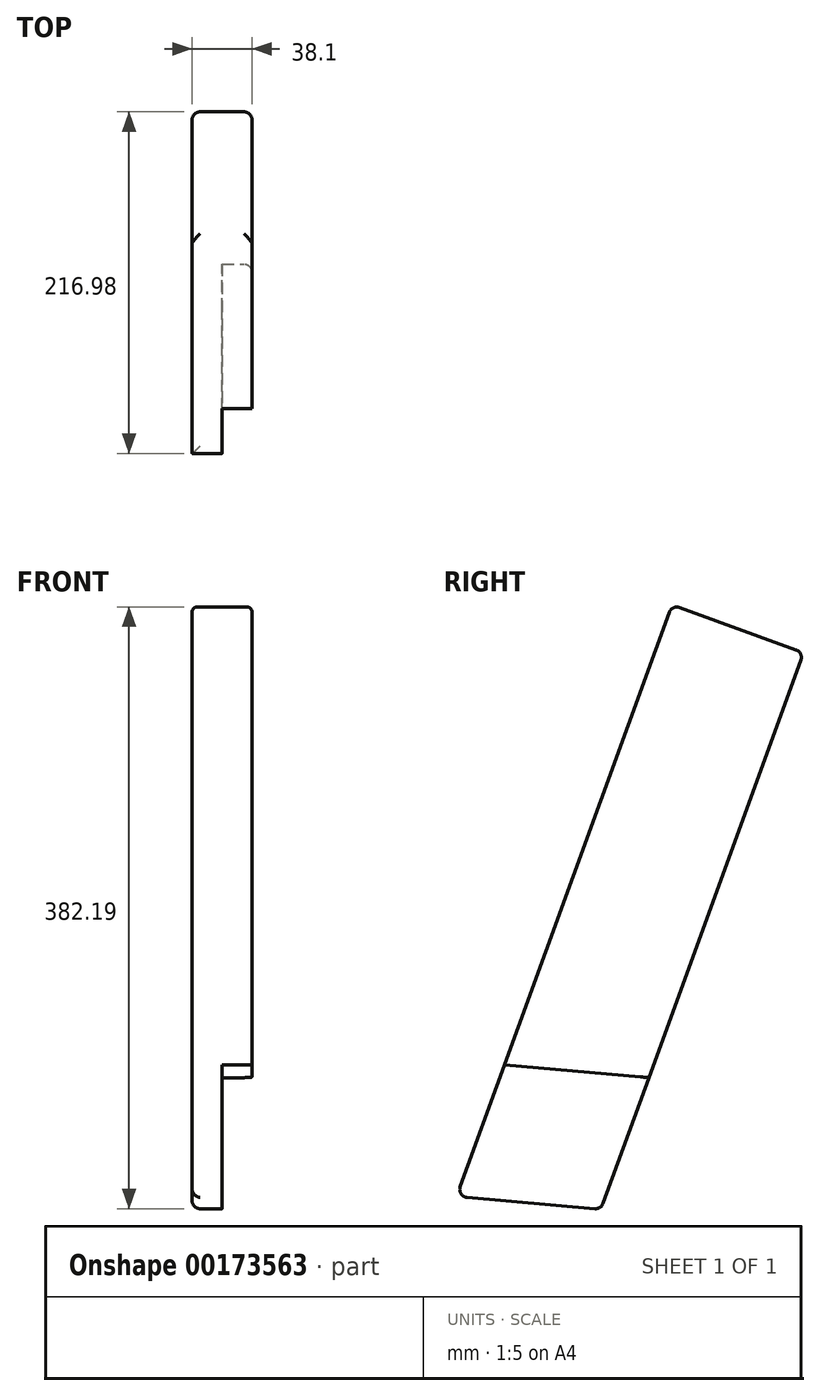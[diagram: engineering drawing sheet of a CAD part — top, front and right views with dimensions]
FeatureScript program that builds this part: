
annotation { "Feature Type Name" : "Feature", "Feature Type Description" : "" }
export const myFeature = defineFeature(function(context is Context, id is Id, definition is map)
    precondition{}
    {
        {
            var Q0;
            Q0=qCreatedBy(makeId("Right.planeOp"),FACE);
            var sketch = newSketch(context, id + "F0", { "sketchPlane" : qUnion([Q0])});
            skLineSegment(sketch, "E0", {"start": v(0, 0) * mm, "end": v(128.68, 353.54) * mm});
            skLineSegment(sketch, "E1", {"start": v(45.14, 383.95) * mm, "end": v(-91.69, 8.02) * mm});
            skLineSegment(sketch, "E2", {"start": v(-91.69, 8.02) * mm, "end": v(0, 0) * mm});
            skLineSegment(sketch, "E3", {"start": v(45.14, 383.95) * mm, "end": v(128.68, 353.54) * mm});
            skSolve(sketch);
        }
        {
            var Q0;
            Q0=makeQuery(id+"F0.imprint","IMPRINT",FACE,{"disambiguationData":[TD([[makeQuery(id+"F0.imprint","IMPRINT",EDGE,{"derivedFrom":sQuery(id+"F0.wireOp",EDGE,"E0")}),1.0]])]});
            extrude(context, id + "F1", {"entities" : qUnion([Q0]), "depth" : 38.1 * mm});
        }
        {
            var Q0;
            Q0=makeQuery(id+"F1.opExtrude","CAP_FACE",FACE,{"disambiguationData":[OSD([sQuery(id+"F0.wireOp",EDGE,"E0"),sQuery(id+"F0.wireOp",EDGE,"aKBehzrh-NYYM-WnDw-YH7h-H0UPKxIf4NXC"),sQuery(id+"F0.wireOp",EDGE,"E1"),sQuery(id+"F0.wireOp",EDGE,"E2"),sQuery(id+"F0.wireOp",EDGE,"E3")])],"isStart":false});
            var sketch = newSketch(context, id + "F2", { "sketchPlane" : qUnion([Q0])});
            skLineSegment(sketch, "E4", {"start": v(34.32, -6.04) * mm, "end": v(0, 0) * mm});
            skLineSegment(sketch, "E5", {"start": v(30.4, 83.54) * mm, "end": v(0, 0) * mm});
            skLineSegment(sketch, "E6", {"start": v(30.4, 83.54) * mm, "end": v(-61.28, 91.56) * mm});
            skLineSegment(sketch, "E7.0", {"start": v(34.32, -6.04) * mm, "end": v(-92.76, 5.07) * mm});
            skLineSegment(sketch, "E8", {"start": v(-61.28, 91.56) * mm, "end": v(-92.76, 5.07) * mm});
            skSolve(sketch);
        }
        {
            var Q0;
            Q0 = qSketchRegion(id + "F2", true);
            extrude(context, id + "F3", {"entities" : qUnion([Q0]), "operationType" : NewBodyOperationType.REMOVE, "oppositeDirection" : true, "depth" : 19.05 * mm});
        }
        {
            var Q0;
            Q0=makeQuery(id+"F1.opExtrude","SWEPT_EDGE",EDGE,{"disambiguationData":[OSD([sQuery(id+"F0.wireOp",EDGE,"aKBehzrh-NYYM-WnDw-YH7h-H0UPKxIf4NXC"),sQuery(id+"F0.wireOp",EDGE,"E3")])]});
            var Q1;
            Q1=makeQuery(id+"F1.opExtrude","CAP_EDGE",EDGE,{"disambiguationData":[OSD([sQuery(id+"F0.wireOp",EDGE,"E3")])],"isStart":true});
            var Q2;
            Q2=makeQuery(id+"F1.opExtrude","CAP_EDGE",EDGE,{"disambiguationData":[OSD([sQuery(id+"F0.wireOp",EDGE,"aKBehzrh-NYYM-WnDw-YH7h-H0UPKxIf4NXC")])],"isStart":false});
            var Q3;
            Q3=makeQuery(id+"F1.opExtrude","CAP_EDGE",EDGE,{"disambiguationData":[OSD([sQuery(id+"F0.wireOp",EDGE,"aKBehzrh-NYYM-WnDw-YH7h-H0UPKxIf4NXC")])],"isStart":true});
            var Q4;
            Q4=makeQuery(id+"F1.opExtrude","CAP_EDGE",EDGE,{"disambiguationData":[OSD([sQuery(id+"F0.wireOp",EDGE,"E0")])],"isStart":true});
            var Q5;
            Q5=makeQuery(id+"F1.opExtrude","CAP_EDGE",EDGE,{"disambiguationData":[OSD([sQuery(id+"F0.wireOp",EDGE,"E0")])],"isStart":false});
            var Q6;
            Q6=makeQuery(id+"F1.opExtrude","SWEPT_EDGE",EDGE,{"disambiguationData":[OSD([sQuery(id+"F0.wireOp",EDGE,"E0"),sQuery(id+"F0.wireOp",EDGE,"E2")])]});
            var Q7;
            Q7=makeQuery(id+"F1.opExtrude","CAP_EDGE",EDGE,{"disambiguationData":[OSD([sQuery(id+"F0.wireOp",EDGE,"E2")])],"isStart":true});
            var Q8;
            Q8=makeQuery(id+"F1.opExtrude","SWEPT_EDGE",EDGE,{"disambiguationData":[OSD([sQuery(id+"F0.wireOp",EDGE,"E1"),sQuery(id+"F0.wireOp",EDGE,"E2")])]});
            var Q9;
            Q9=makeQuery(id+"F1.opExtrude","CAP_EDGE",EDGE,{"disambiguationData":[OSD([sQuery(id+"F0.wireOp",EDGE,"E3")])],"isStart":false});
            fillet(context, id + "F4", {"entities" : qUnion([Q0, Q1, Q2, Q3, Q4, Q5, Q6, Q7, Q8, Q9]), "radius" : 5.08 * mm, "tangentPropagation" : true, "allowEdgeOverflow" : false});
        }
    });
